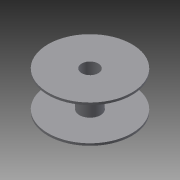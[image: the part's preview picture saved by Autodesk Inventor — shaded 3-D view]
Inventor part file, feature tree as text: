
AUTODESK INVENTOR PART (.ipt)
format: ipt  version: 2013 (Build 170138000, 138)  size: 93,696 bytes
history: native  units: mm
features: extrude x3, sketch x3, projected_geometry x1
ambient origin geometry x8: Origin, YZ Plane, XZ Plane, XY Plane, X Axis, Y Axis, Z Axis, Center Point
bodies: Solid1 (feature_tree)
feature tree (7):
  extrude  "Extrusion1"  Depth=190.0mm
  extrude  "Extrusion2"  Depth=5.0mm
  extrude  "Extrusion3"  Depth=5.0mm TaperAngle=0.0deg
  sketch  "Sketch1"  dims[d0=38.0mm d2=190.0mm]
  sketch  "Sketch2"  dims[d3=5.0mm d4=0.0mm d5=5.0mm]
  sketch  "Sketch3"  dims[d6=75.0mm d7=0.0mm d8=5.0mm d9=0.0mm]
  projected_geometry  "Projected Loop1"
